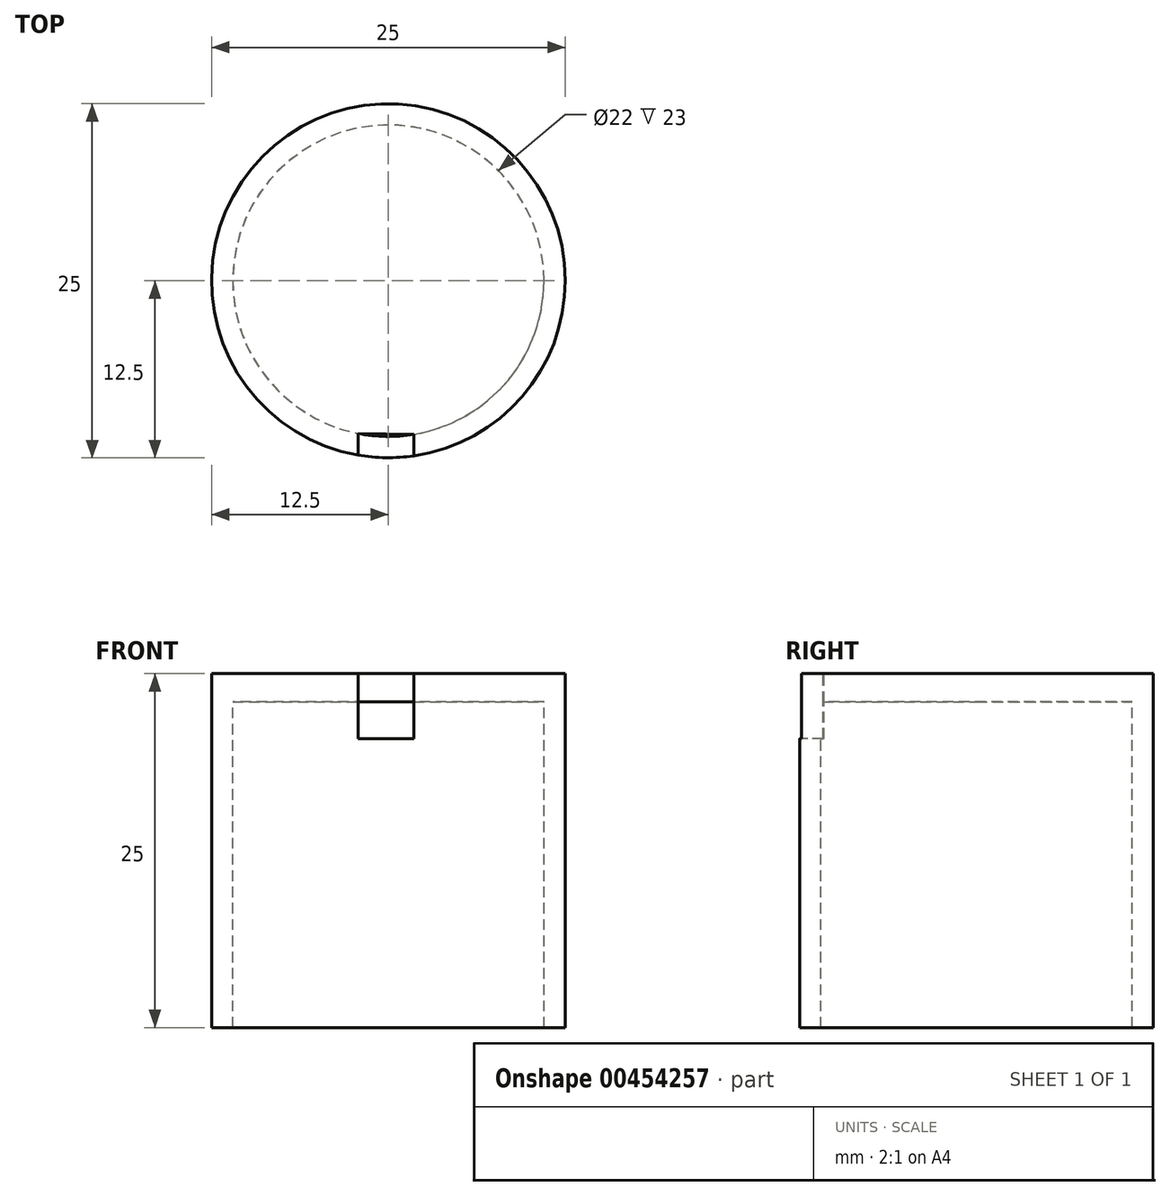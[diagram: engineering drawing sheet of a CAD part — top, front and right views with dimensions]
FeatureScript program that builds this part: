
annotation { "Feature Type Name" : "Feature", "Feature Type Description" : "" }
export const myFeature = defineFeature(function(context is Context, id is Id, definition is map)
    precondition{}
    {
        {
            var Q0;
            Q0=qCreatedBy(makeId("Top.planeOp"),FACE);
            var sketch = newSketch(context, id + "F0", { "sketchPlane" : qUnion([Q0])});
            skCircle(sketch, "E0", {"center": v(0, 0) * mm, "radius": 11 * mm});
            skCircle(sketch, "E1", {"center": v(0, 0) * mm, "radius": 12.5 * mm});
            skSolve(sketch);
        }
        {
            var Q0;
            Q0 = qSketchRegion(id + "F0", true);
            extrude(context, id + "F1", {"entities" : qUnion([Q0]), "oppositeDirection" : true, "depth" : 25 * mm});
        }
        {
            var Q0;
            Q0=qCreatedBy(makeId("Right.planeOp"),FACE);
            cPlane(context, id + "F2", {"entities" : qUnion([Q0]), "cplaneType" : CPlaneType.OFFSET, "offset" : 56.5 * mm, "oppositeDirection" : true, "width" : 150 * mm, "height" : 150 * mm});
        }
        {
            var Q0;
            Q0=qCreatedBy(makeId("Top.planeOp"),FACE);
            var sketch = newSketch(context, id + "F3", { "sketchPlane" : qUnion([Q0])});
            skLineSegment(sketch, "E2.bottom", {"start": v(-2.14, -9.25) * mm, "end": v(1.8, -9.25) * mm});
            skLineSegment(sketch, "E2.top", {"start": v(-2.14, -15.58) * mm, "end": v(1.8, -15.58) * mm});
            skLineSegment(sketch, "E2.left", {"start": v(-2.14, -9.25) * mm, "end": v(-2.14, -15.58) * mm});
            skLineSegment(sketch, "E2.right", {"start": v(1.8, -9.25) * mm, "end": v(1.8, -15.58) * mm});
            skSolve(sketch);
        }
        {
            var Q0;
            Q0 = qSketchRegion(id + "F3", true);
            extrude(context, id + "F4", {"entities" : qUnion([Q0]), "operationType" : NewBodyOperationType.REMOVE, "oppositeDirection" : true, "depth" : 4.6 * mm});
        }
        {
            var Q0;
            Q0=makeQuery(id+"F1.opExtrude","CAP_FACE",FACE,{"disambiguationData":[OSD([sQuery(id+"F0.wireOp",EDGE,"E0"),sQuery(id+"F0.wireOp",EDGE,"E1")])],"isStart":true});
            var sketch = newSketch(context, id + "F5", { "sketchPlane" : qUnion([Q0])});
            skArc(sketch, "E3.0", {"start": v(1.8, -10.85) * mm, "mid": v(0.18, 11) * mm, "end": v(-2.14, -10.79) * mm});
            skLineSegment(sketch, "E4", {"start": v(-2.14, -10.79) * mm, "end": v(1.8, -10.85) * mm});
            skSolve(sketch);
        }
        {
            var Q0;
            Q0 = qSketchRegion(id + "F5", true);
            extrude(context, id + "F6", {"entities" : qUnion([Q0]), "operationType" : NewBodyOperationType.ADD, "oppositeDirection" : true, "depth" : 2 * mm});
        }
    });
